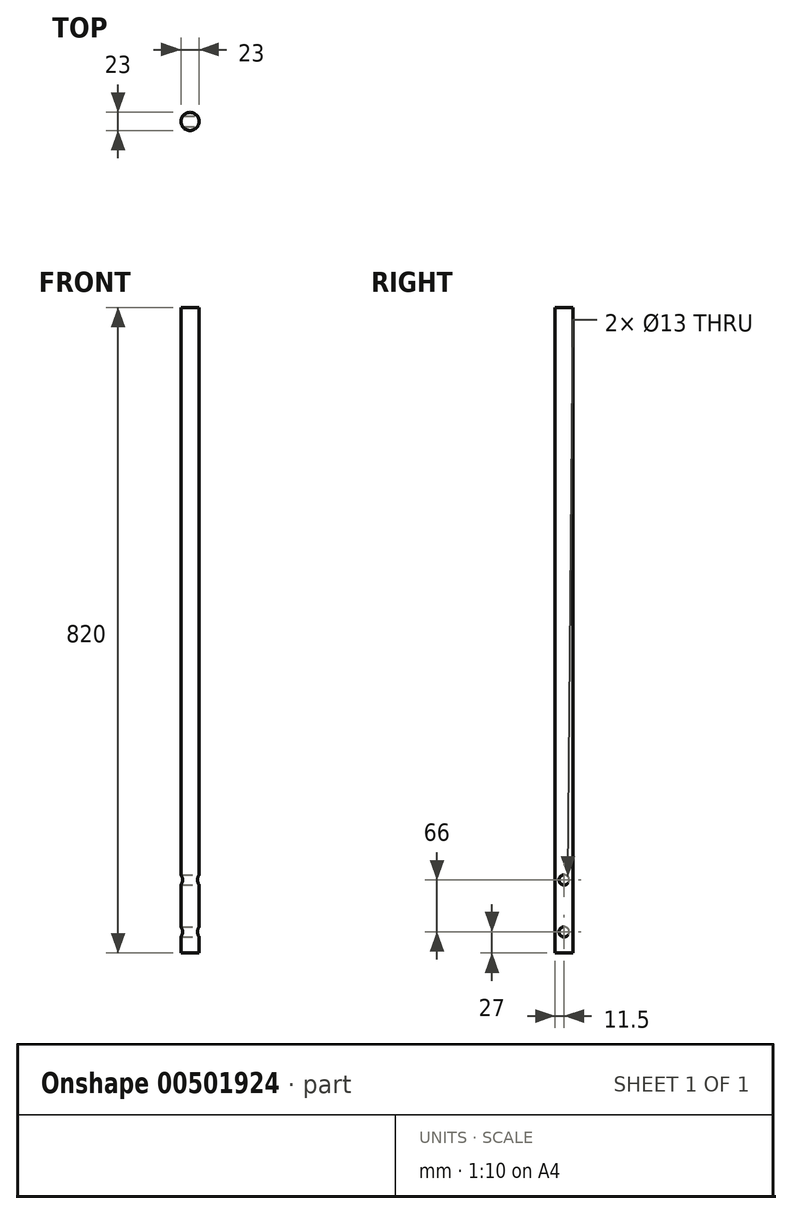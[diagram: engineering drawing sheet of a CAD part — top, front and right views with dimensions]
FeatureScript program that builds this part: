
annotation { "Feature Type Name" : "Feature", "Feature Type Description" : "" }
export const myFeature = defineFeature(function(context is Context, id is Id, definition is map)
    precondition{}
    {
        {
            var Q0;
            Q0=qCreatedBy(makeId("Top.planeOp"),FACE);
            var sketch = newSketch(context, id + "F0", { "sketchPlane" : qUnion([Q0])});
            skCircle(sketch, "E0", {"center": v(0, 0) * mm, "radius": 11.5 * mm});
            skSolve(sketch);
        }
        {
            var Q0;
            Q0=makeQuery(id+"F0.imprint","IMPRINT",FACE,{"disambiguationData":[TD([[makeQuery(id+"F0.imprint","IMPRINT",EDGE,{"derivedFrom":sQuery(id+"F0.wireOp",EDGE,"E0")}),1.0]])]});
            extrude(context, id + "F1", {"entities" : qUnion([Q0]), "depth" : 820 * mm});
        }
        {
            var Q0;
            Q0=qCreatedBy(makeId("Right.planeOp"),FACE);
            var sketch = newSketch(context, id + "F2", { "sketchPlane" : qUnion([Q0])});
            skCircle(sketch, "E1", {"center": v(0, 27) * mm, "radius": 6.5 * mm});
            skCircle(sketch, "E2", {"center": v(0, 93) * mm, "radius": 6.5 * mm});
            skSolve(sketch);
        }
        {
            var Q0;
            Q0 = qSketchRegion(id + "F2", true);
            extrude(context, id + "F3", {"entities" : qUnion([Q0]), "operationType" : NewBodyOperationType.REMOVE, "oppositeDirection" : true, "depth" : 100 * mm, "hasSecondDirection" : true, "secondDirectionOppositeDirection" : false, "secondDirectionDepth" : 25 * mm});
        }
    });
